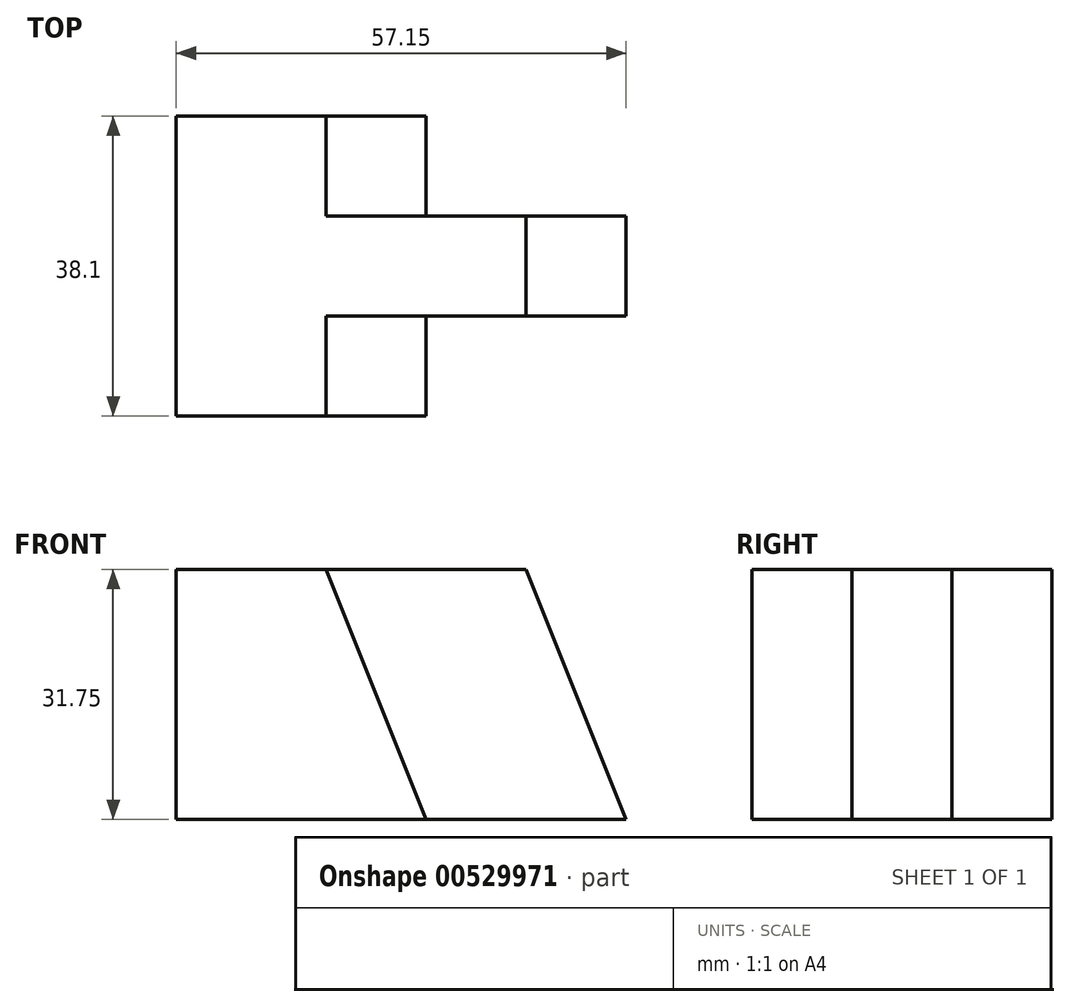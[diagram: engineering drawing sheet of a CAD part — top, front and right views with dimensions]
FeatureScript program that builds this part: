
annotation { "Feature Type Name" : "Feature", "Feature Type Description" : "" }
export const myFeature = defineFeature(function(context is Context, id is Id, definition is map)
    precondition{}
    {
        {
            var Q0;
            Q0=qCreatedBy(makeId("Top.planeOp"),FACE);
            var sketch = newSketch(context, id + "F0", { "sketchPlane" : qUnion([Q0])});
            skLineSegment(sketch, "E0", {"start": v(-64.72, -14.41) * mm, "end": v(-32.97, -14.41) * mm});
            skLineSegment(sketch, "E1", {"start": v(-32.97, -14.41) * mm, "end": v(-32.97, -27.11) * mm});
            skLineSegment(sketch, "E2", {"start": v(-32.97, -27.11) * mm, "end": v(-7.57, -27.11) * mm});
            skLineSegment(sketch, "E3", {"start": v(-7.57, -27.11) * mm, "end": v(-7.57, -39.81) * mm});
            skLineSegment(sketch, "E4", {"start": v(-7.57, -39.81) * mm, "end": v(-32.97, -39.81) * mm});
            skLineSegment(sketch, "E5", {"start": v(-32.97, -39.81) * mm, "end": v(-32.97, -52.51) * mm});
            skLineSegment(sketch, "E6", {"start": v(-32.97, -52.51) * mm, "end": v(-64.72, -52.51) * mm});
            skLineSegment(sketch, "E7", {"start": v(-64.72, -52.51) * mm, "end": v(-64.72, -14.41) * mm});
            skSolve(sketch);
        }
        {
            var Q0;
            Q0=makeQuery(id+"F0.imprint","IMPRINT",FACE,{"disambiguationData":[TD([[makeQuery(id+"F0.imprint","IMPRINT",EDGE,{"derivedFrom":sQuery(id+"F0.wireOp",EDGE,"E0")}),-1.0]])]});
            extrude(context, id + "F1", {"entities" : qUnion([Q0]), "depth" : 31.75 * mm, "offsetDistance" : 25.4 * mm});
        }
        {
            var Q0;
            Q0=makeQuery(id+"F1.opExtrude","SWEPT_FACE",FACE,{"disambiguationData":[OSD([sQuery(id+"F0.wireOp",EDGE,"E4")])]});
            var sketch = newSketch(context, id + "F2", { "sketchPlane" : qUnion([Q0])});
            skLineSegment(sketch, "E8", {"start": v(-7.57, 0) * mm, "end": v(-20.27, 31.75) * mm});
            skSolve(sketch);
        }
        {
            var Q0;
            {var subQ0=sQuery(id+"F2.wireOp",EDGE,"E8");Q0=makeQuery(id+"F2.imprint","IMPRINT",FACE,{"disambiguationData":[TD([[makeQuery(id+"F2.imprint","IMPRINT",EDGE,{"derivedFrom":subQ0}),-1.0]])]});}
            extrude(context, id + "F3", {"entities" : qUnion([Q0]), "operationType" : NewBodyOperationType.REMOVE, "endBound" : BoundingType.THROUGH_ALL, "oppositeDirection" : true, "depth" : 25.4 * mm, "offsetDistance" : 25.4 * mm});
        }
        {
            var Q0;
            Q0=makeQuery(id+"F1.opExtrude","SWEPT_FACE",FACE,{"disambiguationData":[OSD([sQuery(id+"F0.wireOp",EDGE,"E6")])]});
            var sketch = newSketch(context, id + "F4", { "sketchPlane" : qUnion([Q0])});
            skLineSegment(sketch, "E9", {"start": v(-32.97, 0) * mm, "end": v(-45.67, 31.75) * mm});
            skSolve(sketch);
        }
        {
            var Q0;
            {var subQ0=sQuery(id+"F4.wireOp",EDGE,"E9");Q0=makeQuery(id+"F4.imprint","IMPRINT",FACE,{"disambiguationData":[TD([[makeQuery(id+"F4.imprint","IMPRINT",EDGE,{"derivedFrom":subQ0}),-1.0]])]});}
            extrude(context, id + "F5", {"entities" : qUnion([Q0]), "operationType" : NewBodyOperationType.REMOVE, "oppositeDirection" : true, "depth" : 12.7 * mm, "offsetDistance" : 25.4 * mm});
        }
        {
            var Q0;
            Q0=makeQuery(id+"F1.opExtrude","SWEPT_FACE",FACE,{"disambiguationData":[OSD([sQuery(id+"F0.wireOp",EDGE,"E0")])]});
            var sketch = newSketch(context, id + "F6", { "sketchPlane" : qUnion([Q0])});
            skLineSegment(sketch, "E10", {"start": v(32.97, 0) * mm, "end": v(45.67, 31.75) * mm});
            skSolve(sketch);
        }
        {
            var Q0;
            {var subQ0=sQuery(id+"F6.wireOp",EDGE,"E10");Q0=makeQuery(id+"F6.imprint","IMPRINT",FACE,{"disambiguationData":[TD([[makeQuery(id+"F6.imprint","IMPRINT",EDGE,{"derivedFrom":subQ0}),1.0]])]});}
            extrude(context, id + "F7", {"entities" : qUnion([Q0]), "operationType" : NewBodyOperationType.REMOVE, "oppositeDirection" : true, "depth" : 12.7 * mm, "offsetDistance" : 25.4 * mm});
        }
    });
